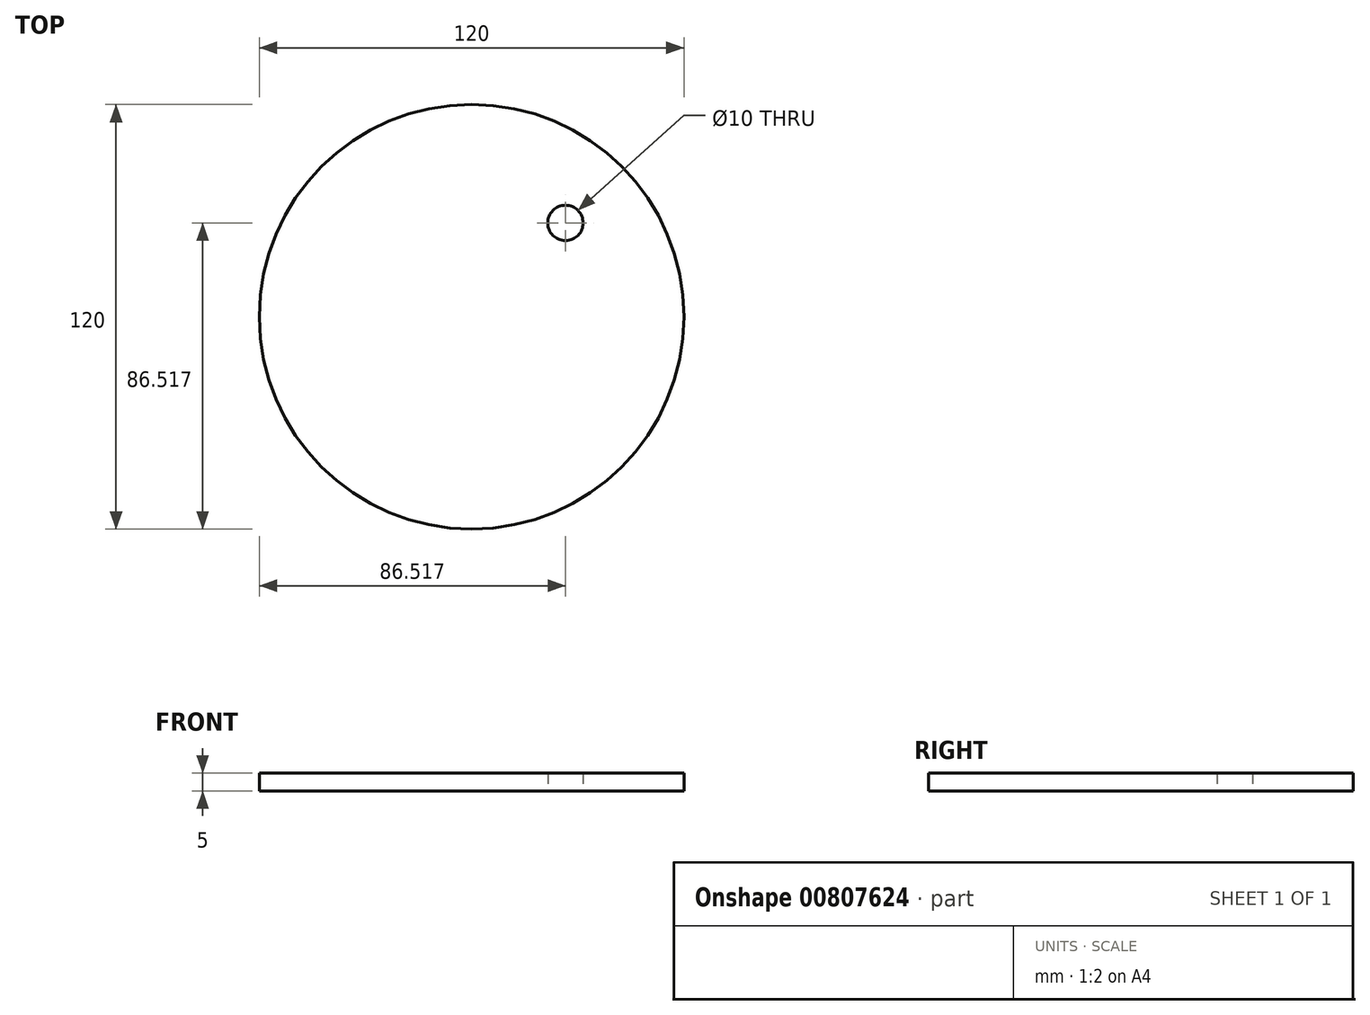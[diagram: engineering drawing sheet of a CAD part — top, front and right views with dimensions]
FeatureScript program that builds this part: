
annotation { "Feature Type Name" : "Feature", "Feature Type Description" : "" }
export const myFeature = defineFeature(function(context is Context, id is Id, definition is map)
    precondition{}
    {
        {
            var Q0;
            Q0=qCreatedBy(makeId("Top.planeOp"),FACE);
            var sketch = newSketch(context, id + "F0", { "sketchPlane" : qUnion([Q0])});
            skCircle(sketch, "E0", {"center": v(0, 0) * mm, "radius": 60 * mm});
            skSolve(sketch);
        }
        {
            var Q0;
            Q0 = qSketchRegion(id + "F0", true);
            extrude(context, id + "F1", {"entities" : qUnion([Q0]), "depth" : 5 * mm, "offsetDistance" : 25 * mm});
        }
        {
            var Q0;
            Q0=makeQuery(id+"F1.opExtrude","CAP_FACE",FACE,{"disambiguationData":[OSD([sQuery(id+"F0.wireOp",EDGE,"E0")])],"isStart":false});
            var sketch = newSketch(context, id + "F2", { "sketchPlane" : qUnion([Q0])});
            skCircle(sketch, "E1", {"center": v(0, 0) * mm, "radius": 37.5 * mm});
            skLineSegment(sketch, "E2", {"start": v(0, 0) * mm, "end": v(86.27, 86.27) * mm});
            skLineSegment(sketch, "E3", {"start": v(0, 0) * mm, "end": v(0, 90) * mm});
            skPoint(sketch, "E4", {"position": v(26.52, 26.52) * mm});
            skSolve(sketch);
        }
        {
            var Q0;
            Q0=sQuery(id+"F2.wireOp",VERTEX,"E4");
            var Q1;
            Q1=makeQuery(id+"F1.opExtrude","SWEPT_BODY",BODY,{"disambiguationData":[OSD([sQuery(id+"F0.wireOp",EDGE,"E0")])]});
            hole(context, id + "F3", {"style" : HoleStyle.SIMPLE, "endStyle" : HoleEndStyle.THROUGH, "holeDiameter" : 10 * mm, "majorDiameter" : 5 * mm, "isTappedThrough" : true, "tappedDepth" : 12 * mm, "tapClearance" : 3, "locations" : qUnion([Q0]), "scope" : qUnion([Q1]), "startStyle" : HoleStartStyle.PART});
        }
        {
            var Q0;
            Q0=qCreatedBy(makeId("Front.planeOp"),FACE);
            var sketch = newSketch(context, id + "F4", { "sketchPlane" : qUnion([Q0])});
            skLineSegment(sketch, "E5", {"start": v(0, 47.32) * mm, "end": v(0, -55.24) * mm, "construction": true});
            skSolve(sketch);
        }
    });
